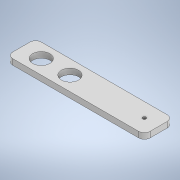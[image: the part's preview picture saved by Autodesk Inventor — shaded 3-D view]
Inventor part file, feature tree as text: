
AUTODESK INVENTOR PART (.ipt)
format: ipt  version: 2022 (Build 260153000, 153)  size: 128,000 bytes
history: native  units: in
note: dims shown in document units (in); Inventor stores cm internally (conversion verified against a paired STEP export)
features: extrude x4, fillet x4, sketch x4
ambient origin geometry x8: Origin, YZ Plane, XZ Plane, XY Plane, X Axis, Y Axis, Z Axis, Center Point
bodies: Solid1 (feature_tree)
feature tree (12):
  extrude  "Extrusion1"  Depth=0.0984in
  extrude  "Extrusion2"  Depth=0.0197in
  extrude  "Extrusion3"  Depth=0.0197in
  extrude  "Extrusion7"  Depth=0.0197in
  fillet  "Fillet2"  Radius=0.0197in
  fillet  "Fillet3"  Radius=0.0118in
  fillet  "Fillet4"  Radius=0.0787in
  fillet  "Fillet5"  Radius=0.0197in
  sketch  "Sketch1"  dims[d0=0.4724in d1=0.0984in]
  sketch  "Sketch2"  dims[d2=0.0197in d3=0.0in d4=0.0591in]
  sketch  "Sketch3"  dims[d5=0.0197in d6=0.0in d7=0.0591in]
  sketch  "Sketch7"  dims[d8=0.0591in d9=0.0591in d10=0.0197in d11=0.0in d21=0.0118in d22=0.0787in d23=0.0in d26=0.0197in d27=0.0197in d28=0.0197in d29=0.0197in]
